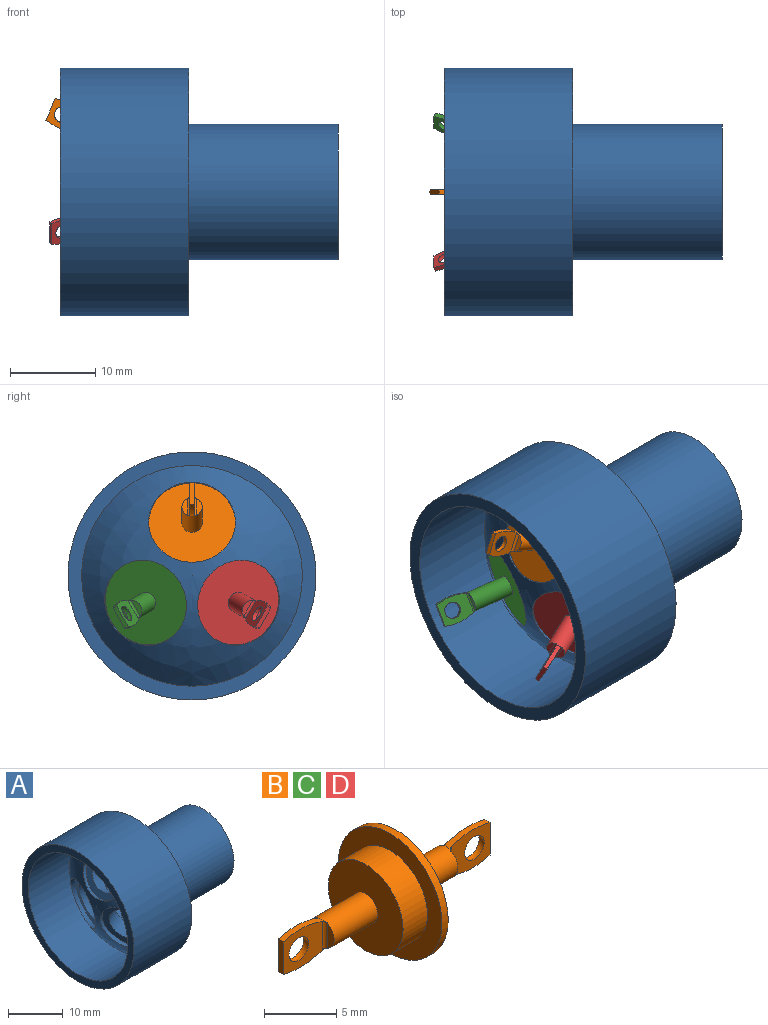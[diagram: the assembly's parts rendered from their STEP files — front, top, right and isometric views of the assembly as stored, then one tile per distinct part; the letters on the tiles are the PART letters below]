
ASSEMBLY  parts=4 mates=3
PART A: 18 faces, bbox 32.5x29x29 mm
  f0: cone r=0mm half-angle=59.8deg, axis (1,0,0), area 60.1mm2, adj f1,f9,f12,f15
  f1: cylinder r=6.67mm len=21.5mm, axis (1,0,0), area 828.2mm2, adj f0,f2,f9,f12,f15
  f2: plane 15.88x15.88mm, normal (1,0,0), area 58.3mm2, adj f1,f3
  f3: cylinder r=7.94mm len=17.51mm, axis (1,0,0), area 873.1mm2, adj f2,f4
  f4: plane 29.05x29.05mm, normal (1,0,0), area 464.8mm2, adj f3,f5
  f5: cylinder r=14.52mm len=29.05mm, axis (1,0,0), area 1371.8mm2, adj f4,f6
  f6: plane 29.05x29.05mm, normal (-1,0,0), area 138.1mm2, adj f5,f7
  f7: cylinder r=12.92mm len=25.85mm, axis (1,0,0), area 876.6mm2, adj f6,f8
  f8: sphere r=16.96mm, area 388.2mm2, adj f7,f11,f14,f17
  f9: cylinder r=3.66mm len=9.4mm, axis (-0.92,0,0.39), area 91.9mm2, adj f0,f1,f10
  f10: plane 10.16x9.36mm, normal (-0.92,0,0.39), area 39mm2, adj f9,f11
  f11: cylinder r=5.08mm len=10.16mm, axis (-0.92,0,0.39), area 27.3mm2, adj f8,f10
  f12: cylinder r=3.66mm len=9.19mm, axis (-0.92,-0.34,-0.19), area 91.9mm2, adj f0,f1,f13
  f13: plane 9.97x9.57mm, normal (-0.92,-0.34,-0.19), area 39mm2, adj f12,f14
  f14: cylinder r=5.08mm len=10.13mm, axis (-0.92,-0.34,-0.19), area 27.3mm2, adj f8,f13
  f15: cylinder r=3.66mm len=9.19mm, axis (-0.92,0.34,-0.19), area 91.9mm2, adj f0,f1,f16
  f16: plane 9.97x9.57mm, normal (-0.92,0.34,-0.19), area 39mm2, adj f15,f17
  f17: cylinder r=5.08mm len=10.13mm, axis (-0.92,0.34,-0.19), area 27.3mm2, adj f8,f16
PART B: 27 faces, bbox 20.3x10.2x10.2 mm
  f0: revolved ~3.97x0.86mm, area 2.1mm2, adj f10,f12,f18,f21,f25,f26
  f1: plane 2.79x0.51mm, normal (1,0,0), area 1.4mm2, adj f2,f3,f13,f16
  f2: revolved ~3.97x0.86mm, area 2.1mm2, adj f1,f4,f13,f16,f23,f24
  f3: revolved ~3.97x0.86mm, area 2.1mm2, adj f1,f4,f13,f16,f23,f24
  f4: cylinder r=1.18mm len=4.95mm, axis (-1,0,0), area 36.2mm2, adj f2,f3,f5,f14,f15,f23,f24
  f5: plane 10.16x10.16mm, normal (1,0,0), area 76.7mm2, adj f4,f6
  f6: cylinder r=5.08mm len=10.16mm, axis (-1,0,0), area 19.5mm2, adj f5,f7
  f7: plane 10.16x10.16mm, normal (-1,0,0), area 39mm2, adj f6,f8
  f8: cylinder r=3.66mm len=7.32mm, axis (-1,0,0), area 54.9mm2, adj f7,f9
  f9: plane 7.32x7.32mm, normal (-1,0,0), area 37.6mm2, adj f8,f10
  f10: cylinder r=1.18mm len=4.36mm, axis (-1,0,0), area 31.8mm2, adj f0,f9,f11,f19,f20,f25,f26
  f11: revolved ~3.97x0.86mm, area 2.1mm2, adj f10,f12,f18,f21,f25,f26
  f12: plane 2.79x0.51mm, normal (-1,0,0), area 1.4mm2, adj f0,f11,f18,f21
  f13: plane 3.82x3.23mm, normal (0,1,0), area 8.6mm2, adj f1,f2,f3,f17,f23
  f14: plane 2.13x0.67mm, normal (1,0,0), area 1mm2, adj f4,f23
  f15: plane 2.13x0.67mm, normal (1,0,0), area 1mm2, adj f4,f24
  f16: plane 3.82x3.23mm, normal (0,-1,0), area 8.6mm2, adj f1,f2,f3,f17,f24
  f17: sphere r=0.99mm, area 3.2mm2, adj f13,f16
  f18: plane 3.82x3.23mm, normal (0,1,0), area 8.6mm2, adj f0,f11,f12,f22,f26
  f19: plane 2.13x0.67mm, normal (-1,0,0), area 1mm2, adj f10,f26
  f20: plane 2.13x0.67mm, normal (-1,0,0), area 1mm2, adj f10,f25
  f21: plane 3.82x3.23mm, normal (0,-1,0), area 8.6mm2, adj f0,f11,f12,f22,f25
  f22: sphere r=0.99mm, area 3.2mm2, adj f18,f21
  f23: cylinder r=0.25mm len=2.43mm, axis (0,0,-1), area 0.9mm2, adj f2,f3,f4,f13,f14
  f24: cylinder r=0.25mm len=2.43mm, axis (0,0,1), area 0.9mm2, adj f2,f3,f4,f15,f16
  f25: cylinder r=0.25mm len=2.43mm, axis (0,0,-1), area 0.9mm2, adj f0,f10,f11,f20,f21
  f26: cylinder r=0.25mm len=2.43mm, axis (0,0,1), area 0.9mm2, adj f0,f10,f11,f18,f19
PART C: same geometry as B
PART D: same geometry as B
PLACE A at identity fixed
PLACE B rot(axis=(0,-1,0),157.1deg) t=(-13.57,0,5.72)mm
PLACE C rot(axis=(0.19,0.95,-0.25),174.1deg) t=(-13.57,4.95,-2.86)mm
PLACE D rot(axis=(-0.19,0.95,0.25),174.1deg) t=(-13.57,-4.95,-2.86)mm
MATE fastened D.f4 <-> A.f12  axis (0.92,0.34,0.19) through (-14.12,-5.16,-2.98)mm
MATE fastened C.f4 <-> A.f15  axis (0.92,-0.34,0.19) through (-14.12,5.16,-2.98)mm
MATE fastened B.f4 <-> A.f9  axis (0.92,0,-0.39) through (-14.12,0,5.95)mm
